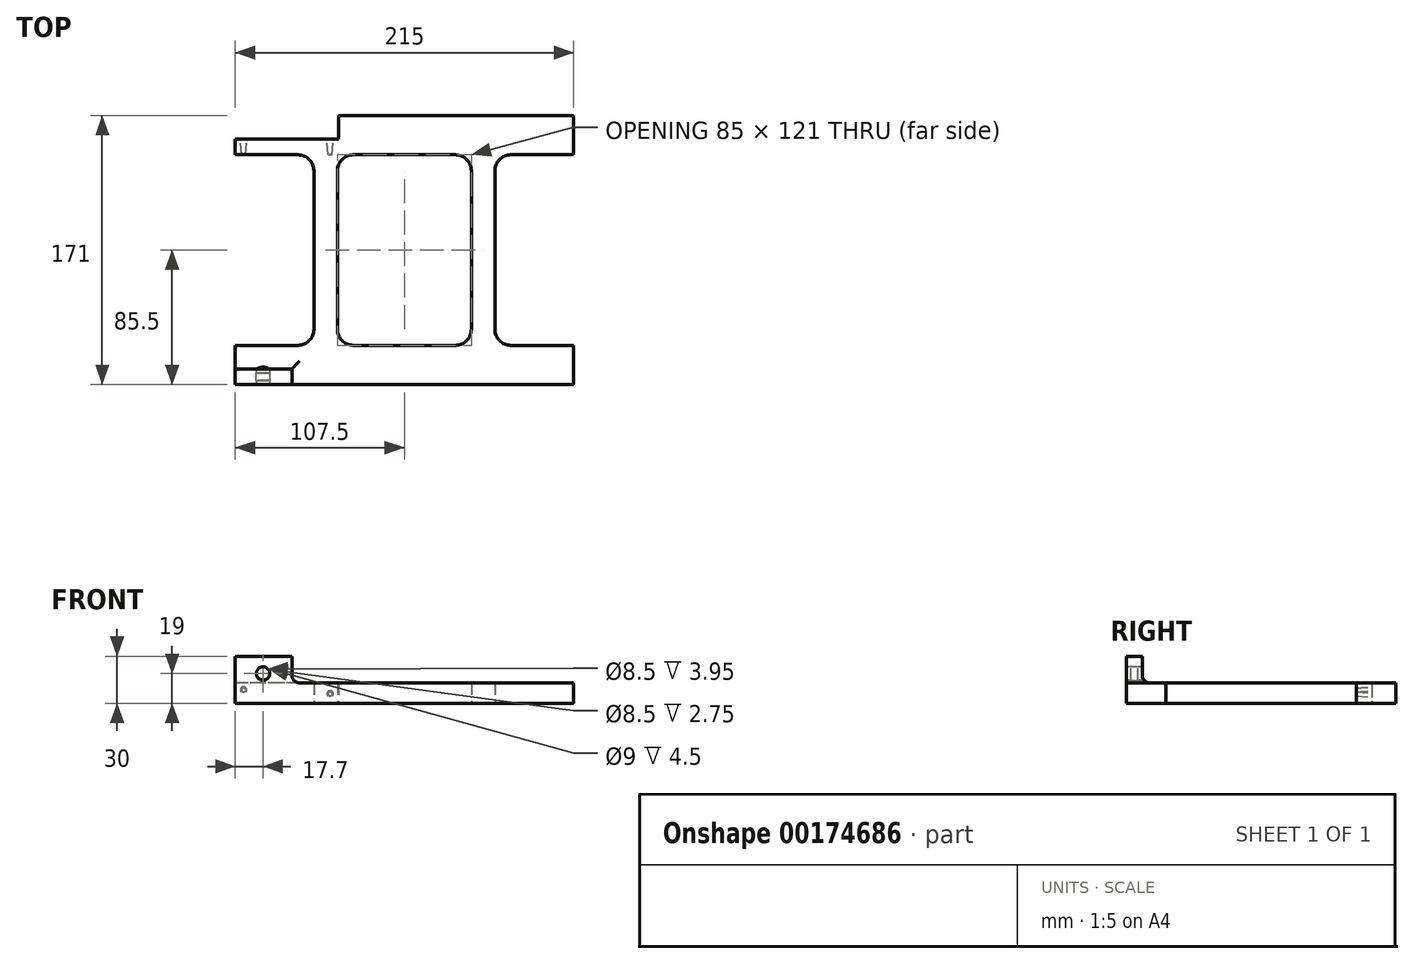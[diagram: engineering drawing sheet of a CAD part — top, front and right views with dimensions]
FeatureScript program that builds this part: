
annotation { "Feature Type Name" : "Feature", "Feature Type Description" : "" }
export const myFeature = defineFeature(function(context is Context, id is Id, definition is map)
    precondition{}
    {
        {
            var Q0;
            Q0=qCreatedBy(makeId("Top.planeOp"),FACE);
            var sketch = newSketch(context, id + "F0", { "sketchPlane" : qUnion([Q0])});
            skLineSegment(sketch, "E0.bottom", {"start": v(-41.7, 70.5) * mm, "end": v(-107.5, 70.5) * mm});
            skLineSegment(sketch, "E0.left", {"start": v(107.5, 70.5) * mm, "end": v(107.5, 60.5) * mm});
            skLineSegment(sketch, "E0.right", {"start": v(-107.5, 70.5) * mm, "end": v(-107.5, 60.5) * mm});
            skPoint(sketch, "E0.middle", {"position": v(0, 0) * mm});
            skLineSegment(sketch, "E1", {"start": v(67.5, 60.5) * mm, "end": v(107.5, 60.5) * mm});
            skLineSegment(sketch, "E2", {"start": v(107.5, -60.5) * mm, "end": v(67.5, -60.5) * mm});
            skLineSegment(sketch, "E3", {"start": v(-57.5, 50.5) * mm, "end": v(-57.5, -50.5) * mm});
            skLineSegment(sketch, "E4", {"start": v(57.5, 50.5) * mm, "end": v(57.5, -50.5) * mm});
            skArc(sketch, "E5.filletArc", {"start": v(67.5, 60.5) * mm, "mid": v(60.43, 57.57) * mm, "end": v(57.5, 50.5) * mm});
            skArc(sketch, "E6.filletArc", {"start": v(57.5, -50.5) * mm, "mid": v(60.43, -57.57) * mm, "end": v(67.5, -60.5) * mm});
            skLineSegment(sketch, "E7", {"start": v(-67.5, 60.5) * mm, "end": v(-107.5, 60.5) * mm});
            skLineSegment(sketch, "E8", {"start": v(-67.5, -60.5) * mm, "end": v(-107.5, -60.5) * mm});
            skArc(sketch, "E9.filletArc", {"start": v(-57.5, 50.5) * mm, "mid": v(-60.43, 57.57) * mm, "end": v(-67.5, 60.5) * mm});
            skArc(sketch, "E10.filletArc", {"start": v(-67.5, -60.5) * mm, "mid": v(-60.43, -57.57) * mm, "end": v(-57.5, -50.5) * mm});
            skLineSegment(sketch, "E11.trimOffspring", {"start": v(-107.5, -60.5) * mm, "end": v(-107.5, -70.5) * mm});
            skLineSegment(sketch, "E12.trimOffspring", {"start": v(107.5, -60.5) * mm, "end": v(107.5, -70.5) * mm});
            skLineSegment(sketch, "E13.bottom", {"start": v(32.5, 60.5) * mm, "end": v(-32.5, 60.5) * mm});
            skLineSegment(sketch, "E13.top", {"start": v(32.5, -60.5) * mm, "end": v(-32.5, -60.5) * mm});
            skLineSegment(sketch, "E13.left", {"start": v(42.5, 50.5) * mm, "end": v(42.5, -50.5) * mm});
            skLineSegment(sketch, "E13.right", {"start": v(-42.5, 50.5) * mm, "end": v(-42.5, -50.5) * mm});
            skArc(sketch, "E14.filletArc", {"start": v(-32.5, 60.5) * mm, "mid": v(-39.57, 57.57) * mm, "end": v(-42.5, 50.5) * mm});
            skArc(sketch, "E15.filletArc", {"start": v(42.5, 50.5) * mm, "mid": v(39.57, 57.57) * mm, "end": v(32.5, 60.5) * mm});
            skArc(sketch, "E16.filletArc", {"start": v(32.5, -60.5) * mm, "mid": v(39.57, -57.57) * mm, "end": v(42.5, -50.5) * mm});
            skArc(sketch, "E17.filletArc", {"start": v(-42.5, -50.5) * mm, "mid": v(-39.57, -57.57) * mm, "end": v(-32.5, -60.5) * mm});
            skLineSegment(sketch, "E18", {"start": v(-41.7, 70.5) * mm, "end": v(-41.7, 85.5) * mm});
            skLineSegment(sketch, "E19", {"start": v(-41.7, 85.5) * mm, "end": v(107.5, 85.5) * mm});
            skLineSegment(sketch, "E20", {"start": v(107.5, 85.5) * mm, "end": v(107.5, 70.5) * mm});
            skLineSegment(sketch, "E21", {"start": v(41.7, -85.5) * mm, "end": v(-107.5, -85.5) * mm});
            skLineSegment(sketch, "E22", {"start": v(-107.5, -85.5) * mm, "end": v(-107.5, -70.5) * mm});
            skLineSegment(sketch, "E23", {"start": v(-107.5, -75.5) * mm, "end": v(-71.5, -75.5) * mm});
            skLineSegment(sketch, "E24", {"start": v(-71.5, -75.5) * mm, "end": v(-71.5, -85.5) * mm});
            skLineSegment(sketch, "E25", {"start": v(41.7, -85.5) * mm, "end": v(107.5, -85.5) * mm});
            skLineSegment(sketch, "E26", {"start": v(107.5, -85.5) * mm, "end": v(107.5, -70.5) * mm});
            skSolve(sketch);
        }
        {
            var Q0;
            Q0 = qSketchRegion(id + "F0", true);
            extrude(context, id + "F1", {"entities" : qUnion([Q0]), "depth" : 13 * mm});
        }
        {
            var Q0;
            Q0=makeQuery(id+"F1.opExtrude","SWEPT_FACE",FACE,{"disambiguationData":[OSD([sQuery(id+"F0.wireOp",EDGE,"E0.bottom")])]});
            cPlane(context, id + "F2", {"entities" : qUnion([Q0]), "cplaneType" : CPlaneType.OFFSET, "offset" : 0 * mm, "width" : 150 * mm, "height" : 150 * mm});
        }
        {
            var Q0;
            Q0=qCreatedBy(id+"F2.planeOp",FACE);
            var sketch = newSketch(context, id + "F3", { "sketchPlane" : qUnion([Q0])});
            skCircle(sketch, "E27", {"center": v(47.2, 6) * mm, "radius": 2 * mm});
            skCircle(sketch, "E28", {"center": v(102.2, 8.5) * mm, "radius": 2 * mm});
            skSolve(sketch);
        }
        {
            var Q0;
            Q0=makeQuery(id+"F3.imprint","IMPRINT",FACE,{"disambiguationData":[TD([[makeQuery(id+"F3.imprint","IMPRINT",EDGE,{"derivedFrom":sQuery(id+"F3.wireOp",EDGE,"E27")}),1.0]])]});
            var Q1;
            Q1=makeQuery(id+"F3.imprint","IMPRINT",FACE,{"disambiguationData":[TD([[makeQuery(id+"F3.imprint","IMPRINT",EDGE,{"derivedFrom":sQuery(id+"F3.wireOp",EDGE,"E28")}),1.0]])]});
            extrude(context, id + "F4", {"entities" : qUnion([Q0, Q1]), "operationType" : NewBodyOperationType.REMOVE, "oppositeDirection" : true, "depth" : 10 * mm, "hasDraft" : true, "draftAngle" : 4 * degree, "draftPullDirection" : true});
        }
        {
            var Q0;
            {var subQ3=sQuery(id+"F0.wireOp",EDGE,"5dVJUSXo-2Qro-aX7G-iqUk-uEtOvwdYrdIJ");Q0=makeQuery(id+"F0.imprint","IMPRINT",FACE,{"disambiguationData":[TD([[makeQuery(id+"F0.imprint","IMPRINT",EDGE,{"derivedFrom":subQ3}),1.0]])]});}
            var Q1;
            {var subQ4=sQuery(id+"F0.wireOp",EDGE,"E23");Q1=makeQuery(id+"F0.imprint","IMPRINT",FACE,{"disambiguationData":[TD([[makeQuery(id+"F0.imprint","IMPRINT",EDGE,{"derivedFrom":subQ4}),-1.0]])]});}
            extrude(context, id + "F5", {"entities" : qUnion([Q0, Q1]), "operationType" : NewBodyOperationType.ADD, "depth" : 30 * mm});
        }
        {
            var Q0;
            Q0=makeQuery(id+"F5.boolean.opBoolean","INTERSECT",EDGE,{"derivedFrom":[makeQuery(id+"F1.opExtrude","CAP_FACE",FACE,{"disambiguationData":[OSD([sQuery(id+"F0.wireOp",EDGE,"E0.bottom"),sQuery(id+"F0.wireOp",EDGE,"E0.top"),sQuery(id+"F0.wireOp",EDGE,"E0.left"),sQuery(id+"F0.wireOp",EDGE,"E0.right"),sQuery(id+"F0.wireOp",EDGE,"E1"),sQuery(id+"F0.wireOp",EDGE,"E2"),sQuery(id+"F0.wireOp",EDGE,"E3"),sQuery(id+"F0.wireOp",EDGE,"E4"),sQuery(id+"F0.wireOp",EDGE,"E5.filletArc"),sQuery(id+"F0.wireOp",EDGE,"E6.filletArc"),sQuery(id+"F0.wireOp",EDGE,"E7"),sQuery(id+"F0.wireOp",EDGE,"E8"),sQuery(id+"F0.wireOp",EDGE,"E9.filletArc"),sQuery(id+"F0.wireOp",EDGE,"E10.filletArc"),sQuery(id+"F0.wireOp",EDGE,"E11.trimOffspring"),sQuery(id+"F0.wireOp",EDGE,"E12.trimOffspring"),sQuery(id+"F0.wireOp",EDGE,"E13.bottom"),sQuery(id+"F0.wireOp",EDGE,"E13.top"),sQuery(id+"F0.wireOp",EDGE,"E13.left"),sQuery(id+"F0.wireOp",EDGE,"E13.right"),sQuery(id+"F0.wireOp",EDGE,"E14.filletArc"),sQuery(id+"F0.wireOp",EDGE,"E15.filletArc"),sQuery(id+"F0.wireOp",EDGE,"E16.filletArc"),sQuery(id+"F0.wireOp",EDGE,"E17.filletArc"),sQuery(id+"F0.wireOp",EDGE,"E18"),sQuery(id+"F0.wireOp",EDGE,"E19"),sQuery(id+"F0.wireOp",EDGE,"E20"),sQuery(id+"F0.wireOp",EDGE,"In8LBco8-EYgv-youu-lZhp-W4htikk0ofGX"),sQuery(id+"F0.wireOp",EDGE,"E21"),sQuery(id+"F0.wireOp",EDGE,"E22")])],"isStart":false}),makeQuery(id+"F5.opExtrude","SWEPT_FACE",FACE,{"disambiguationData":[OSD([sQuery(id+"F0.wireOp",EDGE,"5dVJUSXo-2Qro-aX7G-iqUk-uEtOvwdYrdIJ")])]})]});
            var Q1;
            Q1=makeQuery(id+"F5.boolean.opBoolean","INTERSECT",EDGE,{"derivedFrom":[makeQuery(id+"F1.opExtrude","CAP_FACE",FACE,{"disambiguationData":[OSD([sQuery(id+"F0.wireOp",EDGE,"E0.bottom"),sQuery(id+"F0.wireOp",EDGE,"E0.top"),sQuery(id+"F0.wireOp",EDGE,"E0.left"),sQuery(id+"F0.wireOp",EDGE,"E0.right"),sQuery(id+"F0.wireOp",EDGE,"E1"),sQuery(id+"F0.wireOp",EDGE,"E2"),sQuery(id+"F0.wireOp",EDGE,"E3"),sQuery(id+"F0.wireOp",EDGE,"E4"),sQuery(id+"F0.wireOp",EDGE,"E5.filletArc"),sQuery(id+"F0.wireOp",EDGE,"E6.filletArc"),sQuery(id+"F0.wireOp",EDGE,"E7"),sQuery(id+"F0.wireOp",EDGE,"E8"),sQuery(id+"F0.wireOp",EDGE,"E9.filletArc"),sQuery(id+"F0.wireOp",EDGE,"E10.filletArc"),sQuery(id+"F0.wireOp",EDGE,"E11.trimOffspring"),sQuery(id+"F0.wireOp",EDGE,"E12.trimOffspring"),sQuery(id+"F0.wireOp",EDGE,"E13.bottom"),sQuery(id+"F0.wireOp",EDGE,"E13.top"),sQuery(id+"F0.wireOp",EDGE,"E13.left"),sQuery(id+"F0.wireOp",EDGE,"E13.right"),sQuery(id+"F0.wireOp",EDGE,"E14.filletArc"),sQuery(id+"F0.wireOp",EDGE,"E15.filletArc"),sQuery(id+"F0.wireOp",EDGE,"E16.filletArc"),sQuery(id+"F0.wireOp",EDGE,"E17.filletArc"),sQuery(id+"F0.wireOp",EDGE,"E18"),sQuery(id+"F0.wireOp",EDGE,"E19"),sQuery(id+"F0.wireOp",EDGE,"E20"),sQuery(id+"F0.wireOp",EDGE,"In8LBco8-EYgv-youu-lZhp-W4htikk0ofGX"),sQuery(id+"F0.wireOp",EDGE,"E21"),sQuery(id+"F0.wireOp",EDGE,"E22")])],"isStart":false}),makeQuery(id+"F5.opExtrude","SWEPT_FACE",FACE,{"disambiguationData":[OSD([sQuery(id+"F0.wireOp",EDGE,"XmOfdhmU-dQIR-m3pu-4xWW-DK2uzaVtcaV1")])]})]});
            var Q2;
            Q2=makeQuery(id+"F5.boolean.opBoolean","INTERSECT",EDGE,{"derivedFrom":[makeQuery(id+"F1.opExtrude","CAP_FACE",FACE,{"disambiguationData":[OSD([sQuery(id+"F0.wireOp",EDGE,"E0.bottom"),sQuery(id+"F0.wireOp",EDGE,"E0.top"),sQuery(id+"F0.wireOp",EDGE,"E0.left"),sQuery(id+"F0.wireOp",EDGE,"E0.right"),sQuery(id+"F0.wireOp",EDGE,"E1"),sQuery(id+"F0.wireOp",EDGE,"E2"),sQuery(id+"F0.wireOp",EDGE,"E3"),sQuery(id+"F0.wireOp",EDGE,"E4"),sQuery(id+"F0.wireOp",EDGE,"E5.filletArc"),sQuery(id+"F0.wireOp",EDGE,"E6.filletArc"),sQuery(id+"F0.wireOp",EDGE,"E7"),sQuery(id+"F0.wireOp",EDGE,"E8"),sQuery(id+"F0.wireOp",EDGE,"E9.filletArc"),sQuery(id+"F0.wireOp",EDGE,"E10.filletArc"),sQuery(id+"F0.wireOp",EDGE,"E11.trimOffspring"),sQuery(id+"F0.wireOp",EDGE,"E12.trimOffspring"),sQuery(id+"F0.wireOp",EDGE,"E13.bottom"),sQuery(id+"F0.wireOp",EDGE,"E13.top"),sQuery(id+"F0.wireOp",EDGE,"E13.left"),sQuery(id+"F0.wireOp",EDGE,"E13.right"),sQuery(id+"F0.wireOp",EDGE,"E14.filletArc"),sQuery(id+"F0.wireOp",EDGE,"E15.filletArc"),sQuery(id+"F0.wireOp",EDGE,"E16.filletArc"),sQuery(id+"F0.wireOp",EDGE,"E17.filletArc"),sQuery(id+"F0.wireOp",EDGE,"E18"),sQuery(id+"F0.wireOp",EDGE,"E19"),sQuery(id+"F0.wireOp",EDGE,"E20"),sQuery(id+"F0.wireOp",EDGE,"In8LBco8-EYgv-youu-lZhp-W4htikk0ofGX"),sQuery(id+"F0.wireOp",EDGE,"E21"),sQuery(id+"F0.wireOp",EDGE,"E22")])],"isStart":false}),makeQuery(id+"F5.opExtrude","SWEPT_FACE",FACE,{"disambiguationData":[OSD([sQuery(id+"F0.wireOp",EDGE,"E23")])]})]});
            var Q3;
            Q3=makeQuery(id+"F5.boolean.opBoolean","INTERSECT",EDGE,{"derivedFrom":[makeQuery(id+"F1.opExtrude","CAP_FACE",FACE,{"disambiguationData":[OSD([sQuery(id+"F0.wireOp",EDGE,"E0.bottom"),sQuery(id+"F0.wireOp",EDGE,"E0.top"),sQuery(id+"F0.wireOp",EDGE,"E0.left"),sQuery(id+"F0.wireOp",EDGE,"E0.right"),sQuery(id+"F0.wireOp",EDGE,"E1"),sQuery(id+"F0.wireOp",EDGE,"E2"),sQuery(id+"F0.wireOp",EDGE,"E3"),sQuery(id+"F0.wireOp",EDGE,"E4"),sQuery(id+"F0.wireOp",EDGE,"E5.filletArc"),sQuery(id+"F0.wireOp",EDGE,"E6.filletArc"),sQuery(id+"F0.wireOp",EDGE,"E7"),sQuery(id+"F0.wireOp",EDGE,"E8"),sQuery(id+"F0.wireOp",EDGE,"E9.filletArc"),sQuery(id+"F0.wireOp",EDGE,"E10.filletArc"),sQuery(id+"F0.wireOp",EDGE,"E11.trimOffspring"),sQuery(id+"F0.wireOp",EDGE,"E12.trimOffspring"),sQuery(id+"F0.wireOp",EDGE,"E13.bottom"),sQuery(id+"F0.wireOp",EDGE,"E13.top"),sQuery(id+"F0.wireOp",EDGE,"E13.left"),sQuery(id+"F0.wireOp",EDGE,"E13.right"),sQuery(id+"F0.wireOp",EDGE,"E14.filletArc"),sQuery(id+"F0.wireOp",EDGE,"E15.filletArc"),sQuery(id+"F0.wireOp",EDGE,"E16.filletArc"),sQuery(id+"F0.wireOp",EDGE,"E17.filletArc"),sQuery(id+"F0.wireOp",EDGE,"E18"),sQuery(id+"F0.wireOp",EDGE,"E19"),sQuery(id+"F0.wireOp",EDGE,"E20"),sQuery(id+"F0.wireOp",EDGE,"In8LBco8-EYgv-youu-lZhp-W4htikk0ofGX"),sQuery(id+"F0.wireOp",EDGE,"E21"),sQuery(id+"F0.wireOp",EDGE,"E22")])],"isStart":false}),makeQuery(id+"F5.opExtrude","SWEPT_FACE",FACE,{"disambiguationData":[OSD([sQuery(id+"F0.wireOp",EDGE,"E24")])]})]});
            fillet(context, id + "F6", {"entities" : qUnion([Q0, Q1, Q2, Q3]), "radius" : 5 * mm, "tangentPropagation" : true, "allowEdgeOverflow" : false});
        }
        {
            var Q0;
            {var subQ0=sQuery(id+"F0.wireOp",EDGE,"E21");Q0=makeQuery(id+"F5.boolean.opBoolean","MERGE",FACE,{"derivedFrom":[makeQuery(id+"F1.opExtrude","SWEPT_FACE",FACE,{"disambiguationData":[OSD([subQ0])]}),makeQuery(id+"F5.opExtrude","SWEPT_FACE",FACE,{"disambiguationData":[OSD([subQ0])]})]});}
            cPlane(context, id + "F7", {"entities" : qUnion([Q0]), "cplaneType" : CPlaneType.OFFSET, "offset" : 5 * mm, "oppositeDirection" : true, "width" : 150 * mm, "height" : 150 * mm});
        }
        {
            var Q0;
            Q0=qCreatedBy(id+"F7.planeOp",FACE);
            var sketch = newSketch(context, id + "F8", { "sketchPlane" : qUnion([Q0])});
            skCircle(sketch, "E29", {"center": v(-89.8, 19) * mm, "radius": 4.5 * mm});
            skCircle(sketch, "E30", {"center": v(-89.8, 19) * mm, "radius": 4.25 * mm});
            skSolve(sketch);
        }
        {
            var Q0;
            Q0=makeQuery(id+"F8.imprint","IMPRINT",FACE,{"disambiguationData":[TD([[makeQuery(id+"F8.imprint","IMPRINT",EDGE,{"derivedFrom":sQuery(id+"F8.wireOp",EDGE,"E30")}),1.0]])]});
            var Q1;
            Q1=makeQuery(id+"F47euyNrI3FEx14_1.imprint","IMPRINT",FACE,{"disambiguationData":[TD([[makeQuery(id+"F47euyNrI3FEx14_1.imprint","IMPRINT",EDGE,{"derivedFrom":sQuery(id+"F47euyNrI3FEx14_1.wireOp",EDGE,"NqQoeIfr-Dppt-iodY-T1lp-LGnJyIyBBncX")}),1.0]])]});
            extrude(context, id + "F9", {"entities" : qUnion([Q0, Q1]), "operationType" : NewBodyOperationType.REMOVE, "endBound" : BoundingType.SYMMETRIC, "oppositeDirection" : true, "depth" : 25 * mm});
        }
        {
            var Q0;
            Q0=makeQuery(id+"F8.imprint","IMPRINT",FACE,{"disambiguationData":[TD([[makeQuery(id+"F8.imprint","IMPRINT",EDGE,{"derivedFrom":sQuery(id+"F8.wireOp",EDGE,"E29")}),1.0]])]});
            var Q1;
            Q1=makeQuery(id+"F47euyNrI3FEx14_1.imprint","IMPRINT",FACE,{"disambiguationData":[TD([[makeQuery(id+"F47euyNrI3FEx14_1.imprint","IMPRINT",EDGE,{"derivedFrom":sQuery(id+"F47euyNrI3FEx14_1.wireOp",EDGE,"XOnO3lEe-Rk6w-NvuE-yTiZ-HxiPt3XG3NJC")}),1.0]])]});
            extrude(context, id + "F10", {"entities" : qUnion([Q0, Q1]), "operationType" : NewBodyOperationType.REMOVE, "endBound" : BoundingType.SYMMETRIC, "depth" : 4.5 * mm});
        }
    });
